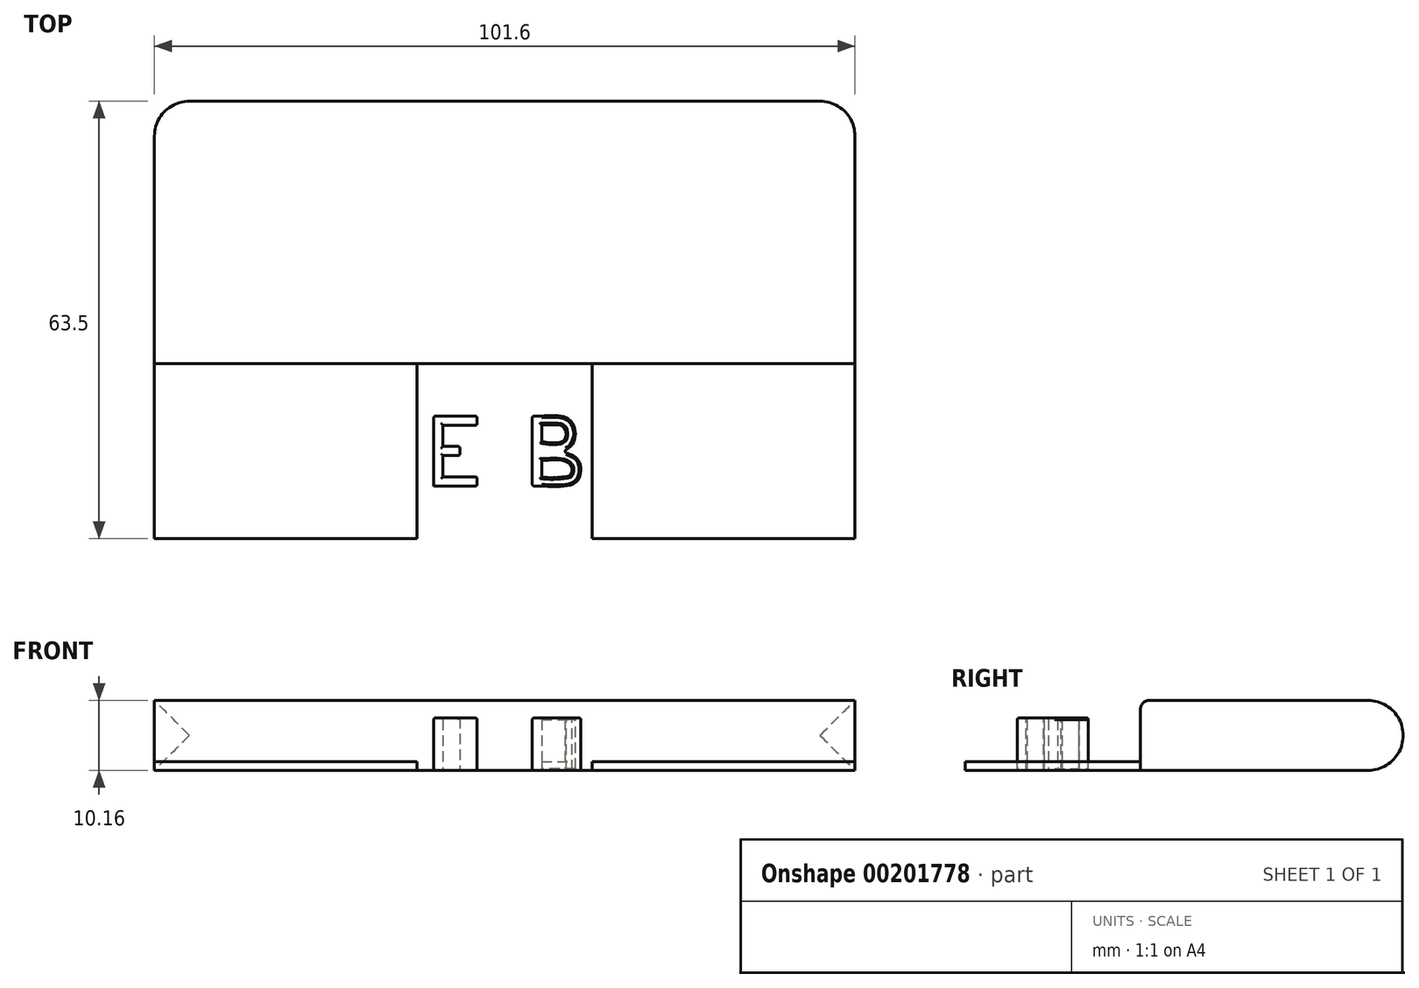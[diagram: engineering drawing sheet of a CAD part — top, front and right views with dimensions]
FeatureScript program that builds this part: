
annotation { "Feature Type Name" : "Feature", "Feature Type Description" : "" }
export const myFeature = defineFeature(function(context is Context, id is Id, definition is map)
    precondition{}
    {
        {
            var Q0;
            Q0=qCreatedBy(makeId("Top.planeOp"),FACE);
            var sketch = newSketch(context, id + "F0", { "sketchPlane" : qUnion([Q0])});
            skLineSegment(sketch, "E0.bottom", {"start": v(-50.8, 50.8) * mm, "end": v(50.8, 50.8) * mm});
            skLineSegment(sketch, "E0.top", {"start": v(-50.8, -50.8) * mm, "end": v(50.8, -50.8) * mm});
            skLineSegment(sketch, "E0.left", {"start": v(-50.8, 50.8) * mm, "end": v(-50.8, -50.8) * mm});
            skLineSegment(sketch, "E0.right", {"start": v(50.8, 50.8) * mm, "end": v(50.8, -50.8) * mm});
            skPoint(sketch, "E0.middle", {"position": v(0, 0) * mm});
            skLineSegment(sketch, "E1.top", {"start": v(-50.8, 12.7) * mm, "end": v(50.8, 12.7) * mm});
            skLineSegment(sketch, "E1.left", {"start": v(-50.8, 50.8) * mm, "end": v(-50.8, 12.7) * mm});
            skLineSegment(sketch, "E1.right", {"start": v(50.8, 50.8) * mm, "end": v(50.8, 12.7) * mm});
            skLineSegment(sketch, "E2.bottom", {"start": v(50.8, -50.8) * mm, "end": v(-50.8, -50.8) * mm});
            skLineSegment(sketch, "E2.top", {"start": v(50.8, -12.7) * mm, "end": v(-50.8, -12.7) * mm});
            skLineSegment(sketch, "E2.left", {"start": v(50.8, -50.8) * mm, "end": v(50.8, -12.7) * mm});
            skLineSegment(sketch, "E2.right", {"start": v(-50.8, -50.8) * mm, "end": v(-50.8, -12.7) * mm});
            skLineSegment(sketch, "E3.bottom", {"start": v(-50.8, 12.7) * mm, "end": v(-12.7, 12.7) * mm});
            skLineSegment(sketch, "E3.top", {"start": v(-50.8, -12.7) * mm, "end": v(-12.7, -12.7) * mm});
            skLineSegment(sketch, "E3.left", {"start": v(-50.8, 12.7) * mm, "end": v(-50.8, -12.7) * mm});
            skLineSegment(sketch, "E3.right", {"start": v(-12.7, 12.7) * mm, "end": v(-12.7, -12.7) * mm});
            skLineSegment(sketch, "E4.bottom", {"start": v(50.8, -12.7) * mm, "end": v(12.7, -12.7) * mm});
            skLineSegment(sketch, "E4.top", {"start": v(50.8, 12.7) * mm, "end": v(12.7, 12.7) * mm});
            skLineSegment(sketch, "E4.left", {"start": v(50.8, -12.7) * mm, "end": v(50.8, 12.7) * mm});
            skLineSegment(sketch, "E4.right", {"start": v(12.7, -12.7) * mm, "end": v(12.7, 12.7) * mm});
            skLineSegment(sketch, "E5", {"start": v(-10.29, 0) * mm, "end": v(-10.29, 5.08) * mm});
            skLineSegment(sketch, "E6", {"start": v(-8.94, 0) * mm, "end": v(-8.94, 5.08) * mm});
            skLineSegment(sketch, "E7", {"start": v(-10.29, 5.08) * mm, "end": v(-4.01, 5.08) * mm});
            skLineSegment(sketch, "E8", {"start": v(-4.01, 5.08) * mm, "end": v(-4.01, 3.73) * mm});
            skLineSegment(sketch, "E9", {"start": v(-4.01, 3.73) * mm, "end": v(-8.94, 3.73) * mm});
            skLineSegment(sketch, "E10", {"start": v(-6.5, 0) * mm, "end": v(-6.5, 0.67) * mm});
            skLineSegment(sketch, "E11", {"start": v(-6.5, 0.67) * mm, "end": v(-8.94, 0.67) * mm});
            skLineSegment(sketch, "E12.MirrorCS", {"start": v(-10.29, 0) * mm, "end": v(-10.29, -5.08) * mm});
            skLineSegment(sketch, "E13.MirrorCS", {"start": v(-10.29, -5.08) * mm, "end": v(-4.01, -5.08) * mm});
            skLineSegment(sketch, "E14.MirrorCS", {"start": v(-8.94, 0) * mm, "end": v(-8.94, -5.08) * mm});
            skLineSegment(sketch, "E15.MirrorCS", {"start": v(-4.01, -3.73) * mm, "end": v(-8.94, -3.73) * mm});
            skLineSegment(sketch, "E16.MirrorCS", {"start": v(-4.01, -5.08) * mm, "end": v(-4.01, -3.73) * mm});
            skLineSegment(sketch, "E17.MirrorCS", {"start": v(-6.5, -0.67) * mm, "end": v(-8.94, -0.67) * mm});
            skLineSegment(sketch, "E18.MirrorCS", {"start": v(-6.5, 0) * mm, "end": v(-6.5, -0.67) * mm});
            skLineSegment(sketch, "E19", {"start": v(0, -4.52) * mm, "end": v(-4.01, -4.52) * mm, "construction": true});
            skLineSegment(sketch, "E20", {"start": v(0, -4.52) * mm, "end": v(4.01, -4.52) * mm, "construction": true});
            skLineSegment(sketch, "E21", {"start": v(4.01, 0) * mm, "end": v(4.01, -5.08) * mm});
            skLineSegment(sketch, "E22", {"start": v(4.01, 0) * mm, "end": v(4.01, 5.08) * mm});
            skLineSegment(sketch, "E23", {"start": v(4.01, 5.08) * mm, "end": v(5.36, 5.08) * mm});
            skLineSegment(sketch, "E24", {"start": v(4.01, -5.08) * mm, "end": v(5.36, -5.08) * mm});
            skFitSpline(sketch, "E25", {"points": [v(5.36, 5.08) * mm, v(8.08, 5.08) * mm, v(9.21, 4.68) * mm, v(9.95, 3.8) * mm, v(10.25, 2.27) * mm, v(9.46, 0.54) * mm, v(8.28, 0) * mm], "startDerivative": vector(13.93, 1) * mm, "endDerivative": vector(-8.38, -2.23) * mm});
            skLineSegment(sketch, "E26", {"start": v(8.28, 0) * mm, "end": v(4.01, 0) * mm});
            skFitSpline(sketch, "E27", {"points": [v(5.36, 3.8) * mm, v(6.37, 3.8) * mm, v(7.64, 3.81) * mm, v(8.54, 3.51) * mm, v(8.9, 2.27) * mm, v(8.28, 1.35) * mm, v(5.36, 1.35) * mm], "startDerivative": vector(6.78, -0.14) * mm, "endDerivative": vector(-14.13, 1.78) * mm});
            skFitSpline(sketch, "E28", {"points": [v(8.28, 0) * mm, v(10.61, -1.2) * mm, v(10.96, -3.45) * mm, v(10.27, -4.57) * mm, v(8.57, -5.1) * mm, v(5.36, -5.08) * mm], "startDerivative": vector(11.82, -5.28) * mm, "endDerivative": vector(-12.14, 0.68) * mm});
            skFitSpline(sketch, "E29", {"points": [v(5.36, -1.3) * mm, v(6.52, -1.3) * mm, v(8.28, -1.35) * mm, v(9.69, -2.18) * mm, v(9.71, -3.14) * mm, v(9.52, -3.54) * mm, v(8.57, -3.76) * mm, v(6.34, -3.86) * mm, v(5.36, -3.76) * mm], "startDerivative": vector(9.01, -0.23) * mm, "endDerivative": vector(-7.5, 1.05) * mm});
            skLineSegment(sketch, "E30", {"start": v(5.36, 3.8) * mm, "end": v(5.36, 1.35) * mm});
            skLineSegment(sketch, "E31", {"start": v(5.36, -1.3) * mm, "end": v(5.36, -3.76) * mm});
            skSolve(sketch);
        }
        {
            var Q0;
            Q0=makeQuery(id+"F0.imprint","IMPRINT",FACE,{"disambiguationData":[TD([[makeQuery(id+"F0.imprint","IMPRINT",EDGE,{"derivedFrom":sQuery(id+"F0.wireOp",EDGE,"E0.bottom")}),-1.0]])]});
            var Q1;
            Q1=makeQuery(id+"F0.imprint","IMPRINT",FACE,{"disambiguationData":[TD([[makeQuery(id+"F0.imprint","IMPRINT",EDGE,{"derivedFrom":sQuery(id+"F0.wireOp",EDGE,"E3.bottom")}),-1.0]])]});
            var Q2;
            Q2=makeQuery(id+"F0.imprint","IMPRINT",FACE,{"disambiguationData":[TD([[makeQuery(id+"F0.imprint","IMPRINT",EDGE,{"derivedFrom":sQuery(id+"F0.wireOp",EDGE,"E2.bottom")}),-1.0]])]});
            var Q3;
            Q3=makeQuery(id+"F0.imprint","IMPRINT",FACE,{"disambiguationData":[TD([[makeQuery(id+"F0.imprint","IMPRINT",EDGE,{"derivedFrom":sQuery(id+"F0.wireOp",EDGE,"E4.bottom")}),-1.0]])]});
            extrude(context, id + "F1", {"entities" : qUnion([Q0, Q1, Q2, Q3]), "depth" : 10.16 * mm});
        }
        {
            var Q0;
            {var subQ10=sQuery(id+"F0.wireOp",EDGE,"E5");Q0=makeQuery(id+"F0.imprint","IMPRINT",FACE,{"disambiguationData":[TD([[makeQuery(id+"F0.imprint","IMPRINT",EDGE,{"derivedFrom":subQ10}),-1.0]])]});}
            var Q1;
            Q1=makeQuery(id+"F0.imprint","IMPRINT",FACE,{"disambiguationData":[TD([[makeQuery(id+"F0.imprint","IMPRINT",EDGE,{"derivedFrom":sQuery(id+"F0.wireOp",EDGE,"E10")}),1.0]])]});
            var Q2;
            {var subQ4=sQuery(id+"F0.wireOp",EDGE,"E8");Q2=makeQuery(id+"F0.imprint","IMPRINT",FACE,{"disambiguationData":[TD([[makeQuery(id+"F0.imprint","IMPRINT",EDGE,{"derivedFrom":subQ4}),-1.0]])]});}
            var Q3;
            {var subQ4=sQuery(id+"F0.wireOp",EDGE,"E15.MirrorCS");Q3=makeQuery(id+"F0.imprint","IMPRINT",FACE,{"disambiguationData":[TD([[makeQuery(id+"F0.imprint","IMPRINT",EDGE,{"derivedFrom":subQ4}),1.0]])]});}
            var Q4;
            Q4=makeQuery(id+"F0.imprint","IMPRINT",FACE,{"disambiguationData":[TD([[makeQuery(id+"F0.imprint","IMPRINT",EDGE,{"derivedFrom":sQuery(id+"F0.wireOp",EDGE,"E21")}),1.0]])]});
            var Q5;
            Q5=makeQuery(id+"F0.imprint","IMPRINT",FACE,{"disambiguationData":[TD([[makeQuery(id+"F0.imprint","IMPRINT",EDGE,{"derivedFrom":sQuery(id+"F0.wireOp",EDGE,"E22")}),-1.0]])]});
            extrude(context, id + "F2", {"entities" : qUnion([Q0, Q1, Q2, Q3, Q4, Q5]), "depth" : 7.62 * mm});
        }
        {
            var Q0;
            Q0=makeQuery(id+"F0.imprint","IMPRINT",FACE,{"disambiguationData":[TD([[makeQuery(id+"F0.imprint","IMPRINT",EDGE,{"derivedFrom":sQuery(id+"F0.wireOp",EDGE,"E1.top")}),-1.0]])]});
            var Q1;
            Q1=makeQuery(id+"F0.imprint","IMPRINT",FACE,{"disambiguationData":[TD([[makeQuery(id+"F0.imprint","IMPRINT",EDGE,{"derivedFrom":sQuery(id+"F0.wireOp",EDGE,"E29")}),-1.0]])]});
            var Q2;
            Q2=makeQuery(id+"F0.imprint","IMPRINT",FACE,{"disambiguationData":[TD([[makeQuery(id+"F0.imprint","IMPRINT",EDGE,{"derivedFrom":sQuery(id+"F0.wireOp",EDGE,"E27")}),-1.0]])]});
            extrude(context, id + "F3", {"entities" : qUnion([Q0, Q1, Q2]), "depth" : 1.27 * mm});
        }
        {
            var Q0;
            Q0=makeQuery(id+"F1.opExtrude","SWEPT_EDGE",EDGE,{"disambiguationData":[OSD([sQuery(id+"F0.wireOp",EDGE,"E2.bottom"),sQuery(id+"F0.wireOp",EDGE,"E2.left")])]});
            var Q1;
            Q1=makeQuery(id+"F1.opExtrude","SWEPT_EDGE",EDGE,{"disambiguationData":[OSD([sQuery(id+"F0.wireOp",EDGE,"E0.bottom"),sQuery(id+"F0.wireOp",EDGE,"E1.right")])]});
            var Q2;
            Q2=makeQuery(id+"F1.opExtrude","SWEPT_EDGE",EDGE,{"disambiguationData":[OSD([sQuery(id+"F0.wireOp",EDGE,"E0.bottom"),sQuery(id+"F0.wireOp",EDGE,"E1.left")])]});
            var Q3;
            Q3=makeQuery(id+"F1.opExtrude","SWEPT_EDGE",EDGE,{"disambiguationData":[OSD([sQuery(id+"F0.wireOp",EDGE,"E2.bottom"),sQuery(id+"F0.wireOp",EDGE,"E2.right")])]});
            var Q4;
            Q4=makeQuery(id+"F1.opExtrude","CAP_EDGE",EDGE,{"disambiguationData":[OSD([sQuery(id+"F0.wireOp",EDGE,"E0.bottom")])],"isStart":false});
            var Q5;
            Q5=makeQuery(id+"F1.opExtrude","CAP_EDGE",EDGE,{"disambiguationData":[OSD([sQuery(id+"F0.wireOp",EDGE,"E0.bottom")])],"isStart":true});
            var Q6;
            Q6=makeQuery(id+"F1.opExtrude","CAP_EDGE",EDGE,{"disambiguationData":[OSD([sQuery(id+"F0.wireOp",EDGE,"E1.right"),sQuery(id+"F0.wireOp",EDGE,"E2.left"),sQuery(id+"F0.wireOp",EDGE,"E4.left")])],"isStart":false});
            var Q7;
            Q7=makeQuery(id+"F1.opExtrude","CAP_EDGE",EDGE,{"disambiguationData":[OSD([sQuery(id+"F0.wireOp",EDGE,"E1.left"),sQuery(id+"F0.wireOp",EDGE,"E2.right"),sQuery(id+"F0.wireOp",EDGE,"E3.left")])],"isStart":false});
            var Q8;
            Q8=makeQuery(id+"F1.opExtrude","CAP_EDGE",EDGE,{"disambiguationData":[OSD([sQuery(id+"F0.wireOp",EDGE,"E1.left"),sQuery(id+"F0.wireOp",EDGE,"E2.right"),sQuery(id+"F0.wireOp",EDGE,"E3.left")])],"isStart":true});
            var Q9;
            Q9=makeQuery(id+"F1.opExtrude","CAP_EDGE",EDGE,{"disambiguationData":[OSD([sQuery(id+"F0.wireOp",EDGE,"E2.bottom")])],"isStart":false});
            var Q10;
            Q10=makeQuery(id+"F1.opExtrude","CAP_EDGE",EDGE,{"disambiguationData":[OSD([sQuery(id+"F0.wireOp",EDGE,"E2.bottom")])],"isStart":true});
            fillet(context, id + "F4", {"entities" : qUnion([Q0, Q1, Q2, Q3, Q4, Q5, Q6, Q7, Q8, Q9, Q10]), "radius" : 5.08 * mm, "tangentPropagation" : true, "allowEdgeOverflow" : false});
        }
        {
            var Q0;
            Q0=makeQuery(id+"F2.opExtrude","CAP_EDGE",EDGE,{"disambiguationData":[OSD([sQuery(id+"F0.wireOp",EDGE,"E15.MirrorCS")])],"isStart":false});
            var Q1;
            Q1=makeQuery(id+"F2.opExtrude","CAP_EDGE",EDGE,{"disambiguationData":[OSD([sQuery(id+"F0.wireOp",EDGE,"E13.MirrorCS")])],"isStart":false});
            var Q2;
            Q2=makeQuery(id+"F2.opExtrude","CAP_EDGE",EDGE,{"disambiguationData":[OSD([sQuery(id+"F0.wireOp",EDGE,"E16.MirrorCS")])],"isStart":false});
            var Q3;
            Q3=makeQuery(id+"F2.opExtrude","CAP_EDGE",EDGE,{"disambiguationData":[OSD([sQuery(id+"F0.wireOp",EDGE,"E14.MirrorCS")])],"isStart":false});
            var Q4;
            Q4=makeQuery(id+"F2.opExtrude","CAP_EDGE",EDGE,{"disambiguationData":[OSD([sQuery(id+"F0.wireOp",EDGE,"E5"),sQuery(id+"F0.wireOp",EDGE,"E12.MirrorCS")])],"isStart":false});
            var Q5;
            Q5=makeQuery(id+"F2.opExtrude","CAP_EDGE",EDGE,{"disambiguationData":[OSD([sQuery(id+"F0.wireOp",EDGE,"E6")])],"isStart":false});
            var Q6;
            Q6=makeQuery(id+"F2.opExtrude","CAP_EDGE",EDGE,{"disambiguationData":[OSD([sQuery(id+"F0.wireOp",EDGE,"E11")])],"isStart":false});
            var Q7;
            Q7=makeQuery(id+"F2.opExtrude","CAP_EDGE",EDGE,{"disambiguationData":[OSD([sQuery(id+"F0.wireOp",EDGE,"E9")])],"isStart":false});
            var Q8;
            Q8=makeQuery(id+"F2.opExtrude","CAP_EDGE",EDGE,{"disambiguationData":[OSD([sQuery(id+"F0.wireOp",EDGE,"E17.MirrorCS")])],"isStart":false});
            var Q9;
            Q9=makeQuery(id+"F2.opExtrude","SWEPT_EDGE",EDGE,{"disambiguationData":[OSD([sQuery(id+"F0.wireOp",EDGE,"E10"),sQuery(id+"F0.wireOp",EDGE,"E11")])]});
            var Q10;
            Q10=makeQuery(id+"F2.opExtrude","SWEPT_EDGE",EDGE,{"disambiguationData":[OSD([sQuery(id+"F0.wireOp",EDGE,"E17.MirrorCS"),sQuery(id+"F0.wireOp",EDGE,"E18.MirrorCS")])]});
            var Q11;
            Q11=makeQuery(id+"F2.opExtrude","SWEPT_EDGE",EDGE,{"disambiguationData":[OSD([sQuery(id+"F0.wireOp",EDGE,"E15.MirrorCS"),sQuery(id+"F0.wireOp",EDGE,"E16.MirrorCS")])]});
            var Q12;
            Q12=makeQuery(id+"F2.opExtrude","SWEPT_EDGE",EDGE,{"disambiguationData":[OSD([sQuery(id+"F0.wireOp",EDGE,"E13.MirrorCS"),sQuery(id+"F0.wireOp",EDGE,"E16.MirrorCS")])]});
            var Q13;
            Q13=makeQuery(id+"F2.opExtrude","CAP_EDGE",EDGE,{"disambiguationData":[OSD([sQuery(id+"F0.wireOp",EDGE,"E7")])],"isStart":false});
            var Q14;
            Q14=makeQuery(id+"F2.opExtrude","SWEPT_FACE",FACE,{"disambiguationData":[OSD([sQuery(id+"F0.wireOp",EDGE,"E7")])]});
            var Q15;
            Q15=makeQuery(id+"F2.opExtrude","SWEPT_FACE",FACE,{"disambiguationData":[OSD([sQuery(id+"F0.wireOp",EDGE,"E8")])]});
            var Q16;
            Q16=makeQuery(id+"F2.opExtrude","CAP_FACE",FACE,{"disambiguationData":[OSD([sQuery(id+"F0.wireOp",EDGE,"E21"),sQuery(id+"F0.wireOp",EDGE,"E22"),sQuery(id+"F0.wireOp",EDGE,"E23"),sQuery(id+"F0.wireOp",EDGE,"E24"),sQuery(id+"F0.wireOp",EDGE,"E25"),sQuery(id+"F0.wireOp",EDGE,"E27"),sQuery(id+"F0.wireOp",EDGE,"E28"),sQuery(id+"F0.wireOp",EDGE,"E29"),sQuery(id+"F0.wireOp",EDGE,"E30"),sQuery(id+"F0.wireOp",EDGE,"E31")])],"isStart":false});
            var Q17;
            Q17=makeQuery(id+"F2.opExtrude","SWEPT_FACE",FACE,{"disambiguationData":[OSD([sQuery(id+"F0.wireOp",EDGE,"E24")])]});
            var Q18;
            Q18=makeQuery(id+"F2.opExtrude","SWEPT_FACE",FACE,{"disambiguationData":[OSD([sQuery(id+"F0.wireOp",EDGE,"E28")])]});
            var Q19;
            Q19=makeQuery(id+"F2.opExtrude","SWEPT_FACE",FACE,{"disambiguationData":[OSD([sQuery(id+"F0.wireOp",EDGE,"E25")])]});
            var Q20;
            Q20=makeQuery(id+"F2.opExtrude","SWEPT_FACE",FACE,{"disambiguationData":[OSD([sQuery(id+"F0.wireOp",EDGE,"E21"),sQuery(id+"F0.wireOp",EDGE,"E22")])]});
            fillet(context, id + "F5", {"entities" : qUnion([Q0, Q1, Q2, Q3, Q4, Q5, Q6, Q7, Q8, Q9, Q10, Q11, Q12, Q13, Q14, Q15, Q16, Q17, Q18, Q19, Q20]), "radius" : 0.25 * mm, "tangentPropagation" : true, "allowEdgeOverflow" : false});
        }
        {
            var Q0;
            Q0=makeQuery(id+"F1.opExtrude","CAP_EDGE",EDGE,{"disambiguationData":[OSD([sQuery(id+"F0.wireOp",EDGE,"E1.top")])],"isStart":false});
            var Q1;
            Q1=makeQuery(id+"F1.opExtrude","CAP_EDGE",EDGE,{"disambiguationData":[OSD([sQuery(id+"F0.wireOp",EDGE,"E4.right")])],"isStart":false});
            var Q2;
            Q2=makeQuery(id+"F1.opExtrude","CAP_EDGE",EDGE,{"disambiguationData":[OSD([sQuery(id+"F0.wireOp",EDGE,"E2.top")])],"isStart":false});
            var Q3;
            Q3=makeQuery(id+"F1.opExtrude","CAP_EDGE",EDGE,{"disambiguationData":[OSD([sQuery(id+"F0.wireOp",EDGE,"E3.right")])],"isStart":false});
            fillet(context, id + "F6", {"entities" : qUnion([Q0, Q1, Q2, Q3]), "radius" : 1.27 * mm, "tangentPropagation" : true, "allowEdgeOverflow" : false});
        }
    });
